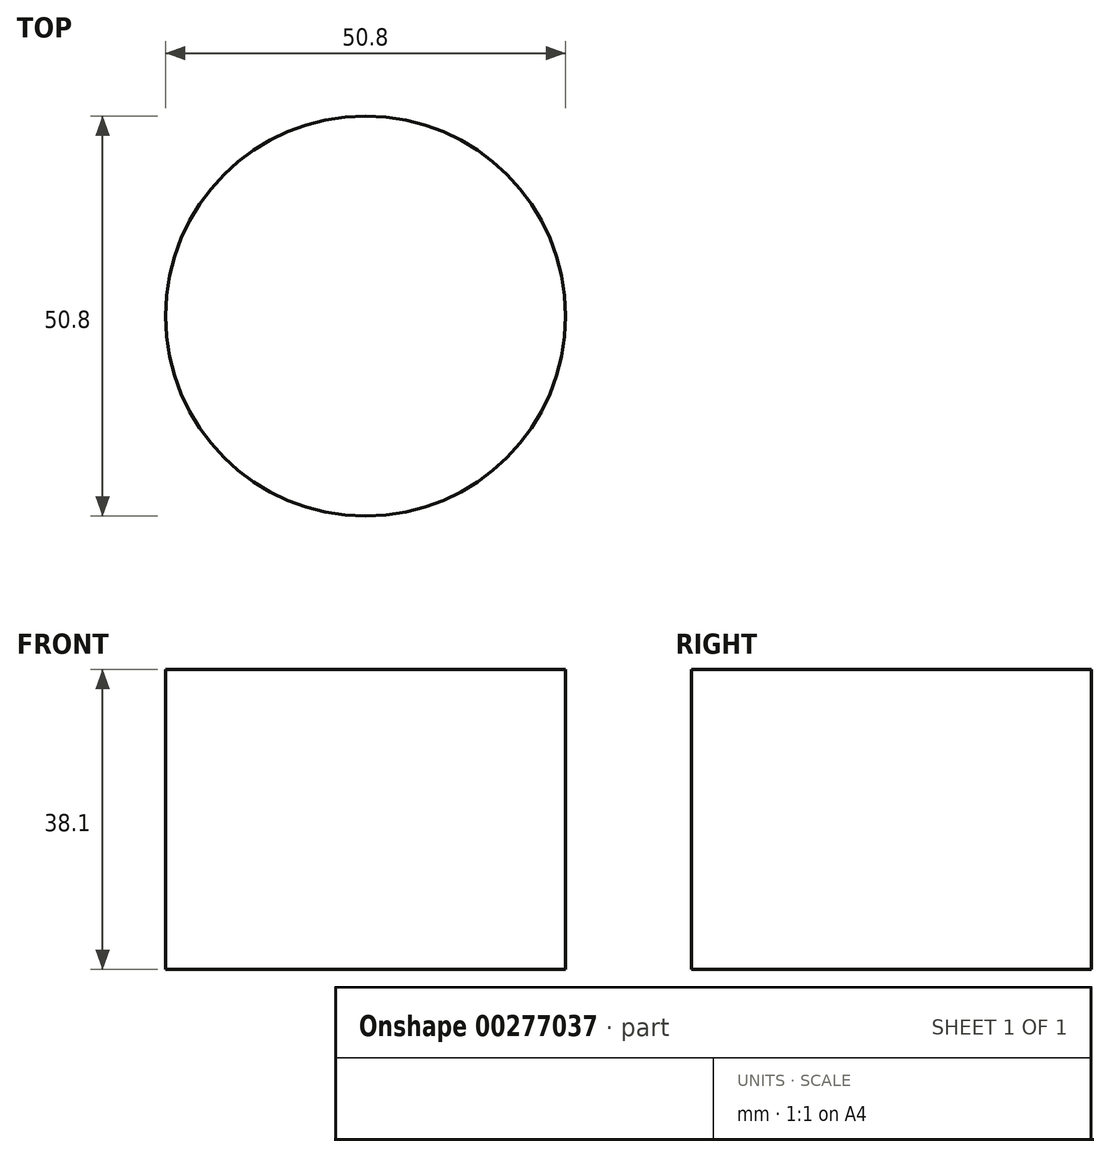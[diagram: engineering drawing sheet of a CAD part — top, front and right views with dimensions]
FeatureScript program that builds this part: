
annotation { "Feature Type Name" : "Feature", "Feature Type Description" : "" }
export const myFeature = defineFeature(function(context is Context, id is Id, definition is map)
    precondition{}
    {
        {
            var Q0;
            Q0=qCreatedBy(makeId("Top.planeOp"),FACE);
            var sketch = newSketch(context, id + "F0", { "sketchPlane" : qUnion([Q0])});
            skCircle(sketch, "E0", {"center": v(-85.35, -30.14) * mm, "radius": 25.4 * mm});
            skSolve(sketch);
        }
        {
            var Q0;
            Q0=makeQuery(id+"F0.imprint","IMPRINT",FACE,{"disambiguationData":[TD([[makeQuery(id+"F0.imprint","IMPRINT",EDGE,{"derivedFrom":sQuery(id+"F0.wireOp",EDGE,"E0")}),1.0]])]});
            extrude(context, id + "F1", {"entities" : qUnion([Q0]), "depth" : 38.1 * mm});
        }
    });
